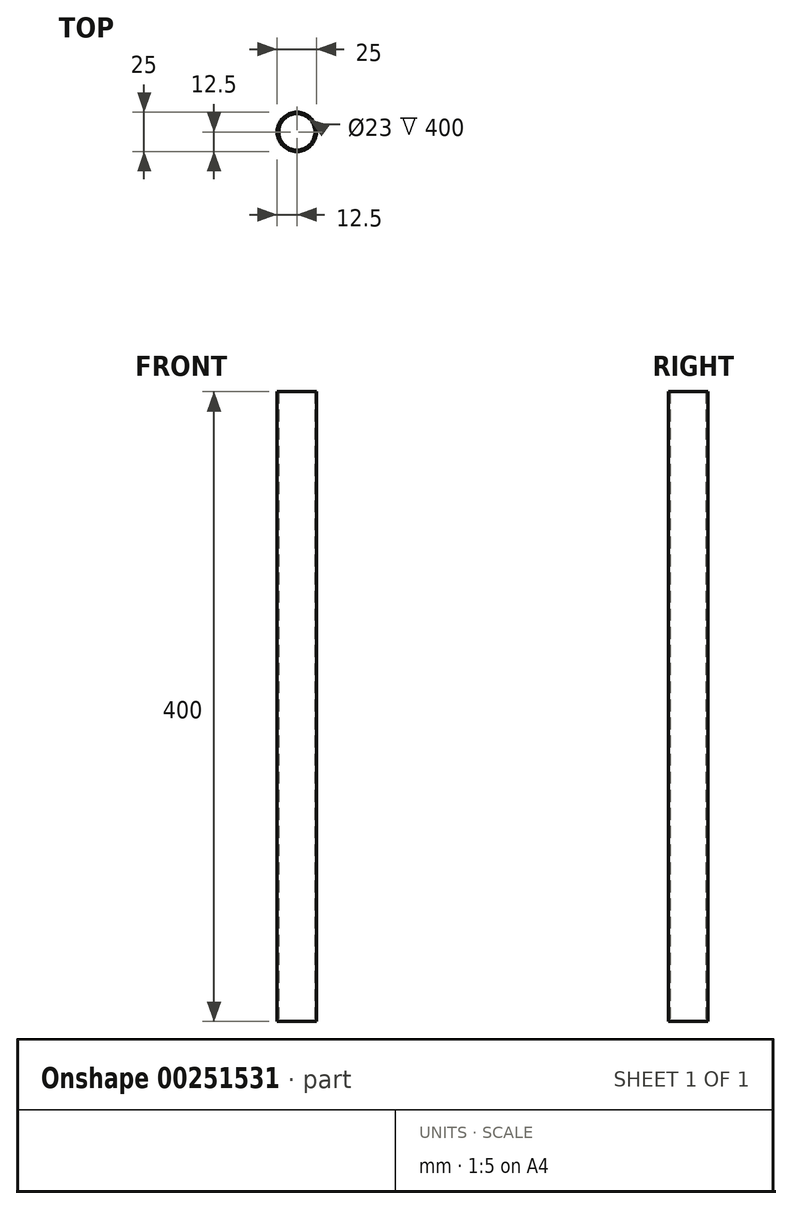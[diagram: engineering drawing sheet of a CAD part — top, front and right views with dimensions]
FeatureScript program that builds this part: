
annotation { "Feature Type Name" : "Feature", "Feature Type Description" : "" }
export const myFeature = defineFeature(function(context is Context, id is Id, definition is map)
    precondition{}
    {
        {
            var Q0;
            Q0=qCreatedBy(makeId("Top.planeOp"),FACE);
            var sketch = newSketch(context, id + "F0", { "sketchPlane" : qUnion([Q0])});
            skCircle(sketch, "E0", {"center": v(0, 0) * mm, "radius": 12.5 * mm});
            skCircle(sketch, "E1", {"center": v(0, 0) * mm, "radius": 11.5 * mm});
            skSolve(sketch);
        }
        {
            var Q0;
            Q0 = qSketchRegion(id + "F0", true);
            extrude(context, id + "F1", {"entities" : qUnion([Q0]), "depth" : 400 * mm});
        }
    });
